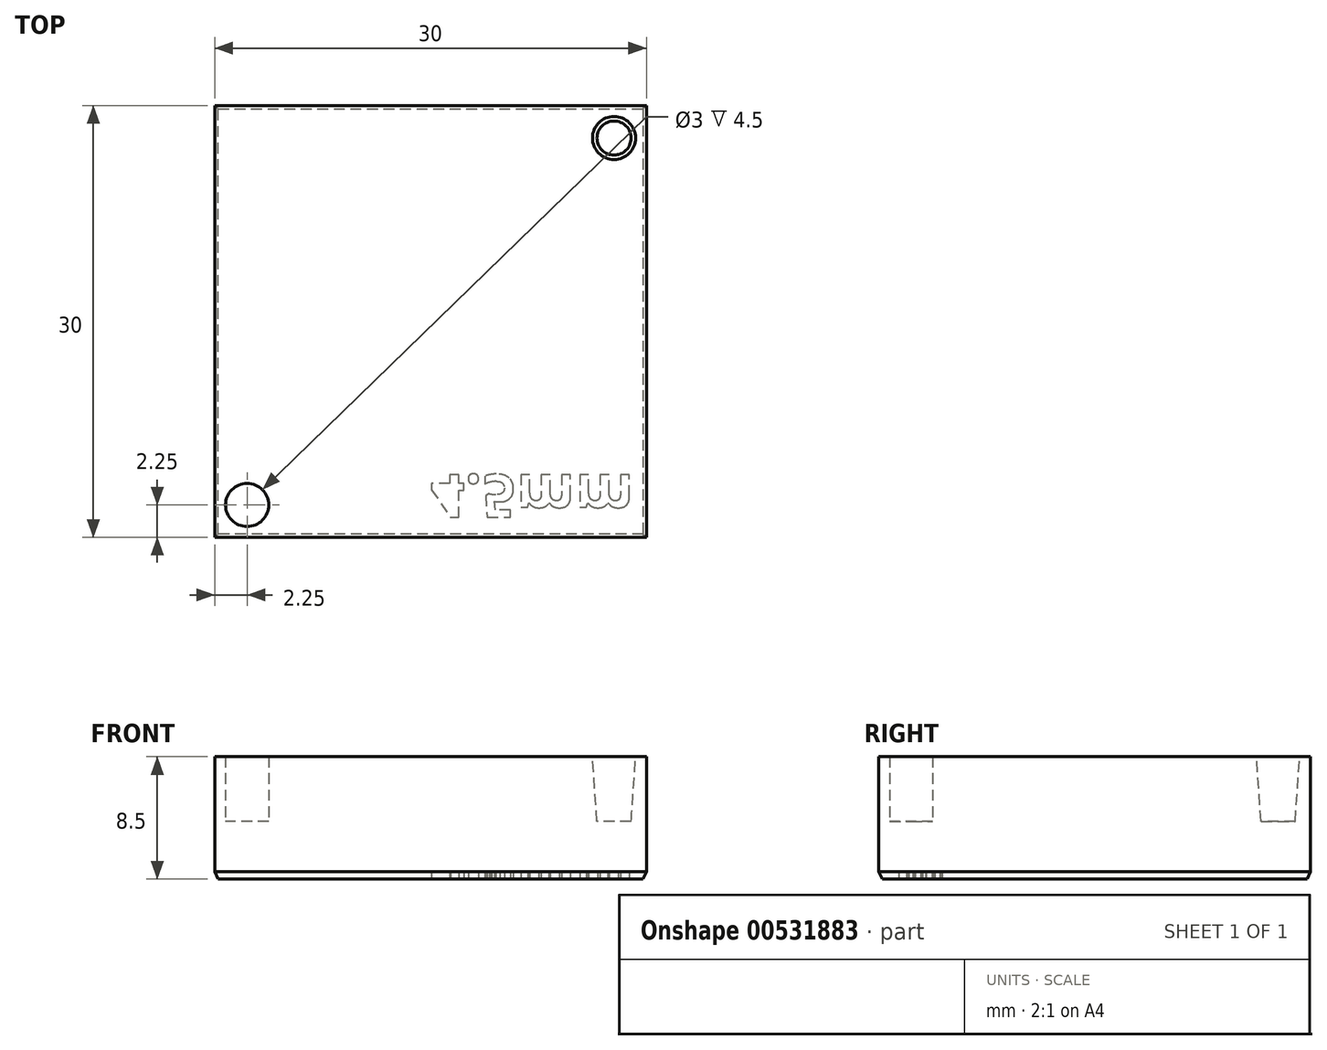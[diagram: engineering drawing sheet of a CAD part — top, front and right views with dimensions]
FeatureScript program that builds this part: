
annotation { "Feature Type Name" : "Feature", "Feature Type Description" : "" }
export const myFeature = defineFeature(function(context is Context, id is Id, definition is map)
    precondition{}
    {
        {
            var Q0;
            Q0=qCreatedBy(makeId("Top.planeOp"),FACE);
            var sketch = newSketch(context, id + "F0", { "sketchPlane" : qUnion([Q0])});
            skLineSegment(sketch, "E0.bottom", {"start": v(-15, -15) * mm, "end": v(15, -15) * mm});
            skLineSegment(sketch, "E0.top", {"start": v(-15, 15) * mm, "end": v(15, 15) * mm});
            skLineSegment(sketch, "E0.left", {"start": v(-15, -15) * mm, "end": v(-15, 15) * mm});
            skLineSegment(sketch, "E0.right", {"start": v(15, -15) * mm, "end": v(15, 15) * mm});
            skSolve(sketch);
        }
        {
            var Q0;
            Q0=makeQuery(id+"F0.imprint","IMPRINT",FACE,{"disambiguationData":[TD([[makeQuery(id+"F0.imprint","IMPRINT",EDGE,{"derivedFrom":sQuery(id+"F0.wireOp",EDGE,"E0.bottom")}),1.0]])]});
            extrude(context, id + "F1", {"entities" : qUnion([Q0]), "depth" : 4 * mm, "offsetDistance" : 25 * mm});
        }
        {
            var Q0;
            Q0=makeQuery(id+"F1.opExtrude","CAP_FACE",FACE,{"disambiguationData":[OSD([sQuery(id+"F0.wireOp",EDGE,"E0.bottom"),sQuery(id+"F0.wireOp",EDGE,"E0.top"),sQuery(id+"F0.wireOp",EDGE,"E0.left"),sQuery(id+"F0.wireOp",EDGE,"E0.right")])],"isStart":false});
            var sketch = newSketch(context, id + "F2", { "sketchPlane" : qUnion([Q0])});
            skCircle(sketch, "E1", {"center": v(-12.75, 12.75) * mm, "radius": 1.5 * mm});
            skCircle(sketch, "E2.MirrorC", {"center": v(12.75, 12.75) * mm, "radius": 1.5 * mm});
            skCircle(sketch, "E3.MirrorC", {"center": v(-12.75, -12.75) * mm, "radius": 1.5 * mm});
            skCircle(sketch, "E4.MirrorC", {"center": v(12.75, -12.75) * mm, "radius": 1.5 * mm});
            skSolve(sketch);
        }
        {
            var Q0;
            Q0=makeQuery(id+"F2.imprint","IMPRINT",FACE,{"disambiguationData":[TD([[makeQuery(id+"F2.imprint","IMPRINT",EDGE,{"derivedFrom":sQuery(id+"F2.wireOp",EDGE,"E1")}),1.0]])]});
            var Q1;
            Q1=makeQuery(id+"F2.imprint","IMPRINT",FACE,{"disambiguationData":[TD([[makeQuery(id+"F2.imprint","IMPRINT",EDGE,{"derivedFrom":sQuery(id+"F2.wireOp",EDGE,"E3.MirrorC")}),-1.0]])]});
            var Q2;
            Q2=makeQuery(id+"F2.imprint","IMPRINT",FACE,{"disambiguationData":[TD([[makeQuery(id+"F2.imprint","IMPRINT",EDGE,{"derivedFrom":sQuery(id+"F2.wireOp",EDGE,"E4.MirrorC")}),1.0]])]});
            var Q3;
            Q3=makeQuery(id+"F2.imprint","IMPRINT",FACE,{"disambiguationData":[TD([[makeQuery(id+"F2.imprint","IMPRINT",EDGE,{"derivedFrom":sQuery(id+"F2.wireOp",EDGE,"E2.MirrorC")}),-1.0]])]});
            extrude(context, id + "F3", {"entities" : qUnion([Q0, Q1, Q2, Q3]), "operationType" : NewBodyOperationType.ADD, "depth" : 4.5 * mm, "offsetDistance" : 25 * mm});
        }
        {
            var Q0;
            Q0=makeQuery(id+"F1.opExtrude","CAP_EDGE",EDGE,{"disambiguationData":[OSD([sQuery(id+"F0.wireOp",EDGE,"E0.bottom")])],"isStart":true});
            var Q1;
            Q1=makeQuery(id+"F1.opExtrude","CAP_EDGE",EDGE,{"disambiguationData":[OSD([sQuery(id+"F0.wireOp",EDGE,"E0.left")])],"isStart":true});
            var Q2;
            Q2=makeQuery(id+"F1.opExtrude","CAP_EDGE",EDGE,{"disambiguationData":[OSD([sQuery(id+"F0.wireOp",EDGE,"E0.right")])],"isStart":true});
            var Q3;
            Q3=makeQuery(id+"F1.opExtrude","CAP_EDGE",EDGE,{"disambiguationData":[OSD([sQuery(id+"F0.wireOp",EDGE,"E0.top")])],"isStart":true});
            chamfer(context, id + "F4", {"entities" : qUnion([Q0, Q1, Q2, Q3]), "chamferType" : ChamferType.OFFSET_ANGLE, "width" : 0.5 * mm, "oppositeDirection" : false, "angle" : 25 * degree, "tangentPropagation" : true});
        }
        {
            var Q0;
            Q0=makeQuery(id+"F3.opExtrude","CAP_EDGE",EDGE,{"disambiguationData":[OSD([sQuery(id+"F2.wireOp",EDGE,"E2.MirrorC")])],"isStart":true});
            var Q1;
            Q1=makeQuery(id+"F3.opExtrude","CAP_EDGE",EDGE,{"disambiguationData":[OSD([sQuery(id+"F2.wireOp",EDGE,"E1")])],"isStart":true});
            var Q2;
            Q2=makeQuery(id+"F3.opExtrude","CAP_EDGE",EDGE,{"disambiguationData":[OSD([sQuery(id+"F2.wireOp",EDGE,"E4.MirrorC")])],"isStart":true});
            var Q3;
            Q3=makeQuery(id+"F3.opExtrude","CAP_EDGE",EDGE,{"disambiguationData":[OSD([sQuery(id+"F2.wireOp",EDGE,"E3.MirrorC")])],"isStart":true});
            chamfer(context, id + "F5", {"entities" : qUnion([Q0, Q1, Q2, Q3]), "chamferType" : ChamferType.OFFSET_ANGLE, "width" : 0.32 * mm, "oppositeDirection" : false, "angle" : 86 * degree, "tangentPropagation" : true});
        }
        {
            var Q0;
            Q0=makeQuery(id+"F1.opExtrude","CAP_FACE",FACE,{"disambiguationData":[OSD([sQuery(id+"F0.wireOp",EDGE,"E0.bottom"),sQuery(id+"F0.wireOp",EDGE,"E0.top"),sQuery(id+"F0.wireOp",EDGE,"E0.left"),sQuery(id+"F0.wireOp",EDGE,"E0.right")])],"isStart":true});
            var sketch = newSketch(context, id + "F6", { "sketchPlane" : qUnion([Q0])});
            skText(sketch, "E5", { "text": "4.5mm", "fontName": "OpenSans-Bold.ttf"});
            const initialGuessF6  = {"E5": [0, 0.01064, 1, 0, 0.003]};
            skSetInitialGuess(sketch, initialGuessF6);
            skSolve(sketch);
        }
        {
            var Q0;
            Q0=makeQuery(id+"F6.imprint","IMPRINT",FACE,{"disambiguationData":[TD([[makeQuery(id+"F6.imprint","IMPRINT",EDGE,{"derivedFrom":sQuery(id+"F6.wireOp",EDGE,"E5.sketch_text.stroke-0")}),-1.0]])]});
            var Q1;
            Q1=makeQuery(id+"F6.imprint","IMPRINT",FACE,{"disambiguationData":[TD([[makeQuery(id+"F6.imprint","IMPRINT",EDGE,{"derivedFrom":sQuery(id+"F6.wireOp",EDGE,"E5.sketch_text.stroke-11")}),1.0]])]});
            var Q2;
            Q2=makeQuery(id+"F6.imprint","IMPRINT",FACE,{"disambiguationData":[TD([[makeQuery(id+"F6.imprint","IMPRINT",EDGE,{"derivedFrom":sQuery(id+"F6.wireOp",EDGE,"E5.sketch_text.stroke-18")}),-1.0]])]});
            var Q3;
            Q3=makeQuery(id+"F6.imprint","IMPRINT",FACE,{"disambiguationData":[TD([[makeQuery(id+"F6.imprint","IMPRINT",EDGE,{"derivedFrom":sQuery(id+"F6.wireOp",EDGE,"E5.sketch_text.stroke-26")}),-1.0]])]});
            var Q4;
            Q4=makeQuery(id+"F6.imprint","IMPRINT",FACE,{"disambiguationData":[TD([[makeQuery(id+"F6.imprint","IMPRINT",EDGE,{"derivedFrom":sQuery(id+"F6.wireOp",EDGE,"E5.sketch_text.stroke-46")}),-1.0]])]});
            var Q5;
            Q5=makeQuery(id+"F6.imprint","IMPRINT",FACE,{"disambiguationData":[TD([[makeQuery(id+"F6.imprint","IMPRINT",EDGE,{"derivedFrom":sQuery(id+"F6.wireOp",EDGE,"E5.sketch_text.stroke-74")}),-1.0]])]});
            extrude(context, id + "F7", {"entities" : qUnion([Q0, Q1, Q2, Q3, Q4, Q5]), "operationType" : NewBodyOperationType.REMOVE, "oppositeDirection" : true, "depth" : 0.5 * mm, "offsetDistance" : 25 * mm});
        }
    });
